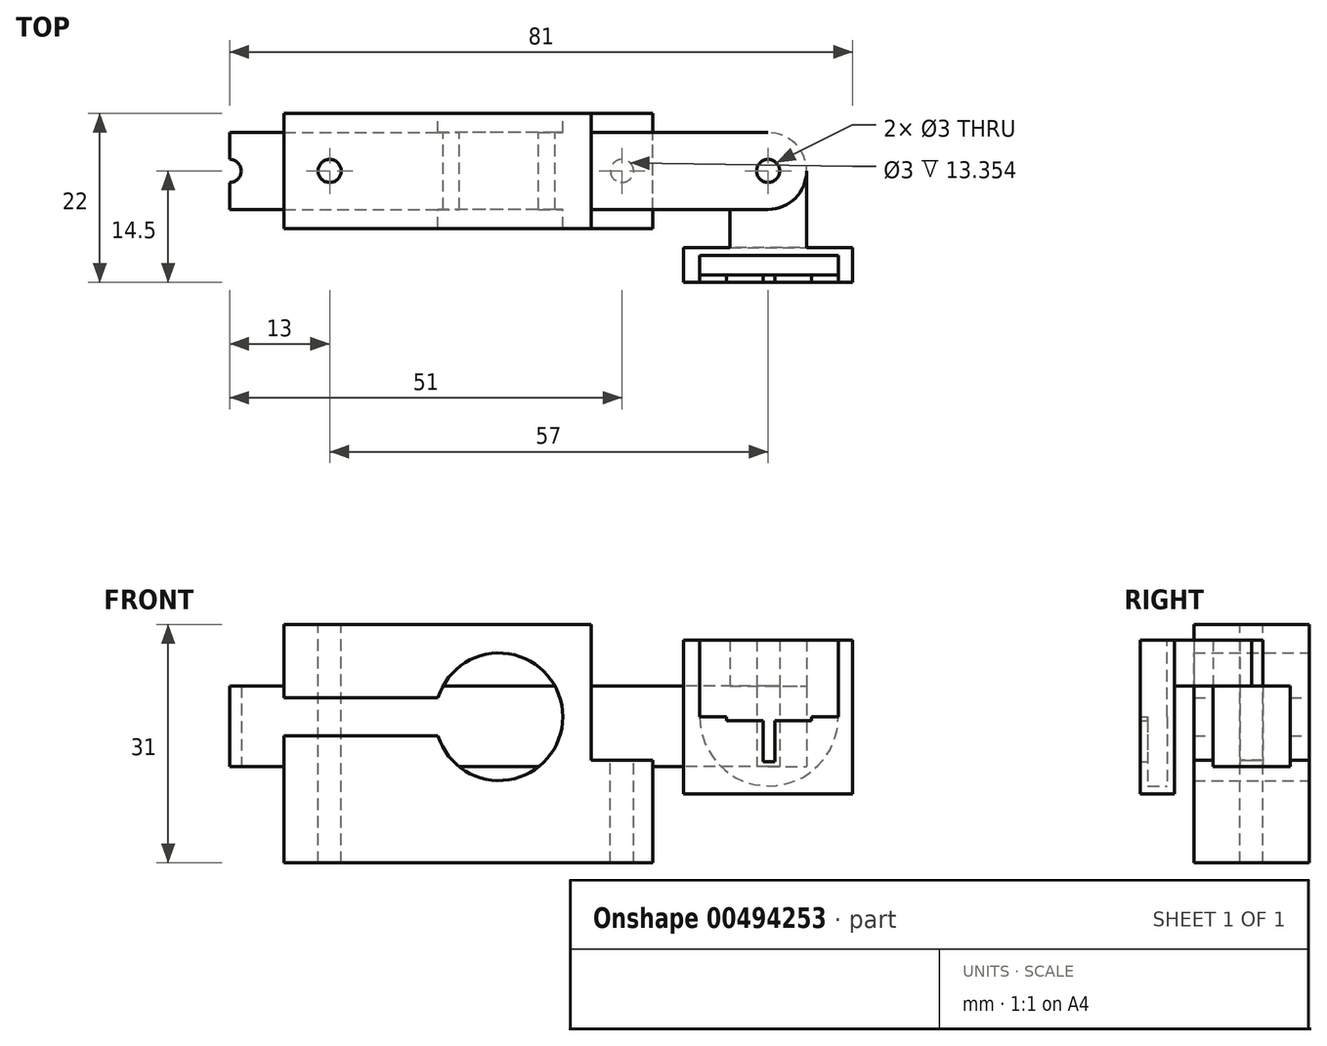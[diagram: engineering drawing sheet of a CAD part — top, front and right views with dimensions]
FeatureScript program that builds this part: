
annotation { "Feature Type Name" : "Feature", "Feature Type Description" : "" }
export const myFeature = defineFeature(function(context is Context, id is Id, definition is map)
    precondition{}
    {
        {
            var Q0;
            Q0=qCreatedBy(makeId("Top.planeOp"),FACE);
            var sketch = newSketch(context, id + "F0", { "sketchPlane" : qUnion([Q0])});
            skCircle(sketch, "E0", {"center": v(0, 0) * mm, "radius": 1.5 * mm});
            skCircle(sketch, "E1", {"center": v(0, 0) * mm, "radius": 3 * mm});
            skSolve(sketch);
        }
        {
            var Q0;
            Q0 = qSketchRegion(id + "F0", true);
            extrude(context, id + "F1", {"entities" : qUnion([Q0]), "depth" : 4 * mm, "offsetDistance" : 25 * mm});
        }
        {
            var Q0;
            Q0=qCreatedBy(makeId("Top.planeOp"),FACE);
            var sketch = newSketch(context, id + "F2", { "sketchPlane" : qUnion([Q0])});
            skLineSegment(sketch, "E2.bottom", {"start": v(35, 5) * mm, "end": v(-35, 5) * mm});
            skLineSegment(sketch, "E2.top", {"start": v(35, -5) * mm, "end": v(-35, -5) * mm});
            skLineSegment(sketch, "E2.left", {"start": v(35, 5) * mm, "end": v(35, -5) * mm});
            skLineSegment(sketch, "E2.right", {"start": v(-35, 5) * mm, "end": v(-35, -5) * mm});
            skPoint(sketch, "E2.middle", {"position": v(0, 0) * mm});
            skArc(sketch, "E3", {"start": v(35, -5) * mm, "mid": v(40, 0) * mm, "end": v(35, 5) * mm});
            skLineSegment(sketch, "E4", {"start": v(0, 15.84) * mm, "end": v(0, -21.96) * mm, "construction": true});
            skPoint(sketch, "E4.startSnap0", {"position": v(0, 5) * mm});
            skPoint(sketch, "E4.endSnap0", {"position": v(0, -5) * mm});
            skArc(sketch, "E5.MirrorCS", {"start": v(-35, -5) * mm, "mid": v(-40, 0) * mm, "end": v(-35, 5) * mm});
            skCircle(sketch, "E6", {"center": v(-35, 0) * mm, "radius": 1.5 * mm});
            skCircle(sketch, "E7.MirrorC", {"center": v(35, 0) * mm, "radius": 1.5 * mm});
            skSolve(sketch);
        }
        {
            var Q0;
            {var subQ5=sQuery(id+"F2.wireOp",EDGE,"E2.bottom");Q0=makeQuery(id+"F2.imprint","IMPRINT",FACE,{"disambiguationData":[TD([[makeQuery(id+"F2.imprint","IMPRINT",EDGE,{"derivedFrom":subQ5}),1.0]])]});}
            var Q1;
            {var subQ0=sQuery(id+"F2.wireOp",EDGE,"E5.MirrorCS");Q1=makeQuery(id+"F2.imprint","IMPRINT",FACE,{"disambiguationData":[TD([[makeQuery(id+"F2.imprint","IMPRINT",EDGE,{"derivedFrom":subQ0}),-1.0]])]});}
            var Q2;
            {var subQ0=sQuery(id+"F2.wireOp",EDGE,"E3");Q2=makeQuery(id+"F2.imprint","IMPRINT",FACE,{"disambiguationData":[TD([[makeQuery(id+"F2.imprint","IMPRINT",EDGE,{"derivedFrom":subQ0}),1.0]])]});}
            extrude(context, id + "F3", {"entities" : qUnion([Q0, Q1, Q2]), "depth" : 4 * mm, "offsetDistance" : 25 * mm});
        }
        {
            var Q0;
            Q0=makeQuery(id+"F3.opExtrude","CAP_FACE",FACE,{"disambiguationData":[OSD([sQuery(id+"F2.wireOp",EDGE,"E2.bottom"),sQuery(id+"F2.wireOp",EDGE,"E2.top"),sQuery(id+"F2.wireOp",EDGE,"E3"),sQuery(id+"F2.wireOp",EDGE,"E5.MirrorCS"),sQuery(id+"F2.wireOp",EDGE,"E6"),sQuery(id+"F2.wireOp",EDGE,"E7.MirrorC")])],"isStart":false});
            var sketch = newSketch(context, id + "F4", { "sketchPlane" : qUnion([Q0])});
            skCircle(sketch, "E8", {"center": v(35, 0) * mm, "radius": 1.5 * mm});
            skArc(sketch, "E9", {"start": v(40, 0) * mm, "mid": v(35, 5) * mm, "end": v(30, 0) * mm});
            skPoint(sketch, "E9.endSnap0", {"position": v(40, 0) * mm});
            skLineSegment(sketch, "E10.bottom", {"start": v(30, 0) * mm, "end": v(40, 0) * mm});
            skLineSegment(sketch, "E10.top", {"start": v(30, -10) * mm, "end": v(40, -10) * mm});
            skLineSegment(sketch, "E10.left", {"start": v(30, 0) * mm, "end": v(30, -10) * mm});
            skLineSegment(sketch, "E10.right", {"start": v(40, 0) * mm, "end": v(40, -10) * mm});
            skSolve(sketch);
        }
        {
            var Q0;
            {var subQ0=sQuery(id+"F4.wireOp",EDGE,"E10.bottom");var subQ3=sQuery(id+"F4.wireOp",EDGE,"E8");var subQ4=makeQuery(id+"F4.imprint","INTERSECT",VERTEX,{"disambiguationData":[OD(0.0)],"derivedFrom":[subQ3,subQ0]});Q0=makeQuery(id+"F4.imprint","IMPRINT",FACE,{"disambiguationData":[TD([[makeQuery(id+"F4.imprint","IMPRINT",EDGE,{"disambiguationData":[TD([[subQ4,-1.0]])],"derivedFrom":subQ3}),1.0]])]});}
            var Q1;
            {var subQ1=sQuery(id+"F4.wireOp",EDGE,"E10.bottom");var subQ6=sQuery(id+"F4.wireOp",EDGE,"E8");var subQ7=makeQuery(id+"F4.imprint","INTERSECT",VERTEX,{"disambiguationData":[OD(0.0)],"derivedFrom":[subQ6,subQ1]});Q1=makeQuery(id+"F4.imprint","IMPRINT",FACE,{"disambiguationData":[TD([[makeQuery(id+"F4.imprint","IMPRINT",EDGE,{"disambiguationData":[TD([[subQ7,1.0]])],"derivedFrom":subQ6}),1.0]])]});}
            var Q2;
            {var subQ2=sQuery(id+"F4.wireOp",EDGE,"E10.top");Q2=makeQuery(id+"F4.imprint","IMPRINT",FACE,{"disambiguationData":[TD([[makeQuery(id+"F4.imprint","IMPRINT",EDGE,{"derivedFrom":subQ2}),1.0]])]});}
            extrude(context, id + "F5", {"entities" : qUnion([Q0, Q1, Q2]), "depth" : 6 * mm, "offsetDistance" : 25 * mm});
        }
        {
            var Q0;
            Q0=makeQuery(id+"F5.opExtrude","SWEPT_FACE",FACE,{"disambiguationData":[OSD([sQuery(id+"F4.wireOp",EDGE,"E10.top")])]});
            var sketch = newSketch(context, id + "F6", { "sketchPlane" : qUnion([Q0])});
            skLineSegment(sketch, "E11.bottom", {"start": v(46, -10) * mm, "end": v(24, -10) * mm});
            skLineSegment(sketch, "E11.top", {"start": v(46, 10) * mm, "end": v(24, 10) * mm});
            skLineSegment(sketch, "E11.left", {"start": v(46, -10) * mm, "end": v(46, 10) * mm});
            skLineSegment(sketch, "E11.right", {"start": v(24, -10) * mm, "end": v(24, 10) * mm});
            skPoint(sketch, "E12", {"position": v(35, -10) * mm});
            skPoint(sketch, "E13", {"position": v(40, 10) * mm});
            skPoint(sketch, "E14", {"position": v(30, 10) * mm});
            skCircle(sketch, "E15", {"center": v(35.12, 0) * mm, "radius": 9 * mm});
            skLineSegment(sketch, "E16", {"start": v(26.12, 0) * mm, "end": v(26.12, 10) * mm});
            skPoint(sketch, "E16.startSnap0", {"position": v(24.12, 0) * mm});
            skLineSegment(sketch, "E17", {"start": v(44.12, 0) * mm, "end": v(44.12, 10) * mm});
            skPoint(sketch, "E17.startSnap0", {"position": v(46.12, 0) * mm});
            skPoint(sketch, "E18", {"position": v(35.12, 9) * mm});
            skSolve(sketch);
        }
        {
            var Q0;
            {var subQ3=sQuery(id+"F6.wireOp",EDGE,"E17");Q0=makeQuery(id+"F6.imprint","IMPRINT",FACE,{"disambiguationData":[TD([[makeQuery(id+"F6.imprint","IMPRINT",EDGE,{"derivedFrom":subQ3}),1.0]])]});}
            var Q1;
            {var subQ3=sQuery(id+"F6.wireOp",EDGE,"E16");Q1=makeQuery(id+"F6.imprint","IMPRINT",FACE,{"disambiguationData":[TD([[makeQuery(id+"F6.imprint","IMPRINT",EDGE,{"derivedFrom":subQ3}),-1.0]])]});}
            var Q2;
            {var subQ0=sQuery(id+"F6.wireOp",EDGE,"E11.top");var subQ1=sQuery(id+"F4.wireOp",EDGE,"E10.top");var subQ2=makeQuery(id+"F5.opExtrude","SWEPT_EDGE",EDGE,{"disambiguationData":[OSD([subQ1,sQuery(id+"F4.wireOp",EDGE,"E10.left")])]});var subQ3=makeQuery(id+"F6.imprint","INTERSECT",VERTEX,{"derivedFrom":[subQ2,subQ0]});var subQ4=makeQuery(id+"F5.opExtrude","SWEPT_EDGE",EDGE,{"disambiguationData":[OSD([subQ1,sQuery(id+"F4.wireOp",EDGE,"E10.right")])]});var subQ5=makeQuery(id+"F6.imprint","INTERSECT",VERTEX,{"derivedFrom":[subQ4,subQ0]});Q2=makeQuery(id+"F6.imprint","IMPRINT",FACE,{"disambiguationData":[TD([[makeQuery(id+"F6.imprint","IMPRINT",EDGE,{"disambiguationData":[TD([[subQ3,-1.0],[subQ5,1.0]])],"derivedFrom":subQ0}),-1.0]])]});}
            var Q3;
            {var subQ1=sQuery(id+"F4.wireOp",EDGE,"E10.top");var subQ6=makeQuery(id+"F5.opExtrude","CAP_EDGE",EDGE,{"disambiguationData":[OSD([subQ1])],"isStart":true});Q3=makeQuery(id+"F6.imprint","IMPRINT",FACE,{"disambiguationData":[TD([[makeQuery(id+"F6.imprint","IMPRINT",EDGE,{"derivedFrom":subQ6}),1.0]])]});}
            var Q4;
            {var subQ0=sQuery(id+"F4.wireOp",EDGE,"E10.top");var subQ1=makeQuery(id+"F5.opExtrude","CAP_EDGE",EDGE,{"disambiguationData":[OSD([subQ0])],"isStart":true});Q4=makeQuery(id+"F6.imprint","IMPRINT",FACE,{"disambiguationData":[TD([[makeQuery(id+"F6.imprint","IMPRINT",EDGE,{"derivedFrom":subQ1}),-1.0]])]});}
            extrude(context, id + "F7", {"entities" : qUnion([Q0, Q1, Q2, Q3, Q4]), "operationType" : NewBodyOperationType.ADD, "depth" : 1 * mm, "offsetDistance" : 25 * mm});
        }
        {
            var Q0;
            Q0=makeQuery(id+"F6.imprint","IMPRINT",FACE,{"disambiguationData":[TD([[makeQuery(id+"F6.imprint","IMPRINT",EDGE,{"derivedFrom":sQuery(id+"F6.wireOp",EDGE,"E11.bottom")}),-1.0]])]});
            extrude(context, id + "F8", {"entities" : qUnion([Q0]), "operationType" : NewBodyOperationType.ADD, "depth" : 3.5 * mm, "offsetDistance" : 25 * mm});
        }
        {
            var Q0;
            Q0=makeQuery(id+"F8.opExtrude","CAP_FACE",FACE,{"disambiguationData":[OSD([sQuery(id+"F6.wireOp",EDGE,"E11.bottom"),sQuery(id+"F6.wireOp",EDGE,"E11.top"),sQuery(id+"F6.wireOp",EDGE,"E11.left"),sQuery(id+"F6.wireOp",EDGE,"E11.right"),sQuery(id+"F6.wireOp",EDGE,"E15"),sQuery(id+"F6.wireOp",EDGE,"E16"),sQuery(id+"F6.wireOp",EDGE,"E17")])],"isStart":false});
            var sketch = newSketch(context, id + "F9", { "sketchPlane" : qUnion([Q0])});
            skLineSegment(sketch, "E19", {"start": v(26.12, 0) * mm, "end": v(44.12, 0) * mm, "construction": true});
            skLineSegment(sketch, "E20", {"start": v(35.12, -9) * mm, "end": v(35.12, -5.85) * mm, "construction": true});
            skLineSegment(sketch, "E21", {"start": v(34.37, -5.85) * mm, "end": v(35.87, -5.85) * mm});
            skLineSegment(sketch, "E22", {"start": v(34.37, -5.85) * mm, "end": v(34.37, 5.25) * mm});
            skLineSegment(sketch, "E23", {"start": v(34.37, 5.25) * mm, "end": v(35.87, 5.25) * mm});
            skLineSegment(sketch, "E24", {"start": v(35.87, 5.25) * mm, "end": v(35.87, -5.85) * mm});
            skLineSegment(sketch, "E25.bottom", {"start": v(40.67, -0.5) * mm, "end": v(29.57, -0.5) * mm});
            skLineSegment(sketch, "E25.top", {"start": v(40.67, 0.5) * mm, "end": v(29.57, 0.5) * mm});
            skLineSegment(sketch, "E25.left", {"start": v(40.67, -0.5) * mm, "end": v(40.67, 0.5) * mm});
            skLineSegment(sketch, "E25.right", {"start": v(29.57, -0.5) * mm, "end": v(29.57, 0.5) * mm});
            skPoint(sketch, "E25.middle", {"position": v(35.12, 0) * mm});
            skLineSegment(sketch, "E26", {"start": v(26.12, 0) * mm, "end": v(44.12, 0) * mm});
            skSolve(sketch);
        }
        {
            var Q0;
            {var subQ1=sQuery(id+"F9.wireOp",EDGE,"E21");Q0=makeQuery(id+"F9.imprint","IMPRINT",FACE,{"disambiguationData":[TD([[makeQuery(id+"F9.imprint","IMPRINT",EDGE,{"derivedFrom":subQ1}),-1.0]])]});}
            var Q1;
            Q1=makeQuery(id+"F9.imprint","IMPRINT",FACE,{"disambiguationData":[TD([[makeQuery(id+"F9.imprint","IMPRINT",EDGE,{"derivedFrom":makeQuery(id+"F8.opExtrude","CAP_EDGE",EDGE,{"disambiguationData":[OSD([sQuery(id+"F6.wireOp",EDGE,"E11.bottom")])],"isStart":false})}),-1.0]])]});
            extrude(context, id + "F10", {"entities" : qUnion([Q0, Q1]), "operationType" : NewBodyOperationType.ADD, "depth" : 1 * mm, "offsetDistance" : 25 * mm});
        }
        {
            var Q0;
            Q0=makeQuery(id+"F3.opExtrude","CAP_FACE",FACE,{"disambiguationData":[OSD([sQuery(id+"F2.wireOp",EDGE,"E2.bottom"),sQuery(id+"F2.wireOp",EDGE,"E2.top"),sQuery(id+"F2.wireOp",EDGE,"E3"),sQuery(id+"F2.wireOp",EDGE,"E5.MirrorCS"),sQuery(id+"F2.wireOp",EDGE,"E6"),sQuery(id+"F2.wireOp",EDGE,"E7.MirrorC")])],"isStart":true});
            extrude(context, id + "F11", {"entities" : qUnion([Q0]), "operationType" : NewBodyOperationType.ADD, "depth" : 6.5 * mm, "offsetDistance" : 25 * mm});
        }
        {
            var Q0;
            Q0=qCreatedBy(makeId("Front.planeOp"),FACE);
            var sketch = newSketch(context, id + "F12", { "sketchPlane" : qUnion([Q0])});
            skArc(sketch, "E27", {"start": v(-7.91, -2.5) * mm, "mid": v(8.3, 0) * mm, "end": v(-7.91, 2.5) * mm});
            skLineSegment(sketch, "E28", {"start": v(0, 12) * mm, "end": v(12, 12) * mm});
            skLineSegment(sketch, "E29", {"start": v(12, 12) * mm, "end": v(12, 0) * mm});
            skLineSegment(sketch, "E30", {"start": v(12, 0) * mm, "end": v(12, -12) * mm});
            skLineSegment(sketch, "E31", {"start": v(12, -12) * mm, "end": v(0, -12) * mm});
            skLineSegment(sketch, "E32", {"start": v(0, -12) * mm, "end": v(-27.91, -12) * mm});
            skLineSegment(sketch, "E33", {"start": v(0, 12) * mm, "end": v(-27.91, 12) * mm});
            skLineSegment(sketch, "E34", {"start": v(-27.91, 12) * mm, "end": v(-27.91, 2.5) * mm});
            skLineSegment(sketch, "E35", {"start": v(-7.91, 2.5) * mm, "end": v(-27.91, 2.5) * mm});
            skLineSegment(sketch, "E36", {"start": v(-7.91, -2.5) * mm, "end": v(-27.91, -2.5) * mm});
            skLineSegment(sketch, "E37.trimOffspring", {"start": v(-27.91, -2.5) * mm, "end": v(-27.91, -12) * mm});
            skSolve(sketch);
        }
        {
            var Q0;
            Q0=makeQuery(id+"F12.imprint","IMPRINT",FACE,{"disambiguationData":[TD([[makeQuery(id+"F12.imprint","IMPRINT",EDGE,{"derivedFrom":sQuery(id+"F12.wireOp",EDGE,"E27")}),-1.0]])]});
            extrude(context, id + "F13", {"entities" : qUnion([Q0]), "depth" : 15 * mm, "offsetDistance" : 25 * mm, "symmetric" : true});
        }
        {
            var Q0;
            Q0=makeQuery(id+"F13.opExtrude","SWEPT_FACE",FACE,{"disambiguationData":[OSD([sQuery(id+"F12.wireOp",EDGE,"E28"),sQuery(id+"F12.wireOp",EDGE,"E33")])]});
            var sketch = newSketch(context, id + "F14", { "sketchPlane" : qUnion([Q0])});
            skCircle(sketch, "E38", {"center": v(-22, 0) * mm, "radius": 1.5 * mm});
            skSolve(sketch);
        }
        {
            var Q0;
            Q0=makeQuery(id+"F14.imprint","IMPRINT",FACE,{"disambiguationData":[TD([[makeQuery(id+"F14.imprint","IMPRINT",EDGE,{"derivedFrom":sQuery(id+"F14.wireOp",EDGE,"E38")}),1.0]])]});
            extrude(context, id + "F15", {"entities" : qUnion([Q0]), "operationType" : NewBodyOperationType.REMOVE, "oppositeDirection" : true, "depth" : 31.6 * mm, "offsetDistance" : 25 * mm});
        }
        {
            var Q0;
            Q0=makeQuery(id+"F13.opExtrude","SWEPT_FACE",FACE,{"disambiguationData":[OSD([sQuery(id+"F12.wireOp",EDGE,"E29"),sQuery(id+"F12.wireOp",EDGE,"E30")])]});
            var sketch = newSketch(context, id + "F16", { "sketchPlane" : qUnion([Q0])});
            skLineSegment(sketch, "E39", {"start": v(-7.5, -5.65) * mm, "end": v(7.5, -5.65) * mm});
            skLineSegment(sketch, "E40", {"start": v(7.5, -5.65) * mm, "end": v(7.5, -12) * mm});
            skLineSegment(sketch, "E41", {"start": v(7.5, -12) * mm, "end": v(-7.5, -12) * mm});
            skLineSegment(sketch, "E42", {"start": v(-7.5, -12) * mm, "end": v(-7.5, -5.65) * mm});
            skSolve(sketch);
        }
        {
            var Q0;
            Q0=makeQuery(id+"F16.imprint","IMPRINT",FACE,{"disambiguationData":[TD([[makeQuery(id+"F16.imprint","IMPRINT",EDGE,{"derivedFrom":sQuery(id+"F16.wireOp",EDGE,"E39")}),-1.0]])]});
            extrude(context, id + "F17", {"entities" : qUnion([Q0]), "operationType" : NewBodyOperationType.ADD, "depth" : 8 * mm, "offsetDistance" : 25 * mm});
        }
        {
            var Q0;
            Q0=makeQuery(id+"F17.opExtrude","SWEPT_FACE",FACE,{"disambiguationData":[OSD([sQuery(id+"F16.wireOp",EDGE,"E39")])]});
            var sketch = newSketch(context, id + "F18", { "sketchPlane" : qUnion([Q0])});
            skCircle(sketch, "E43", {"center": v(16, 0) * mm, "radius": 1.5 * mm});
            skSolve(sketch);
        }
        {
            var Q0;
            Q0=makeQuery(id+"F18.imprint","IMPRINT",FACE,{"disambiguationData":[TD([[makeQuery(id+"F18.imprint","IMPRINT",EDGE,{"derivedFrom":sQuery(id+"F18.wireOp",EDGE,"E43")}),1.0]])]});
            extrude(context, id + "F19", {"entities" : qUnion([Q0]), "operationType" : NewBodyOperationType.REMOVE, "oppositeDirection" : true, "depth" : 25 * mm, "offsetDistance" : 25 * mm});
        }
        {
            var Q0;
            Q0=makeQuery(id+"F17.boolean.opBoolean","MERGE",FACE,{"derivedFrom":[makeQuery(id+"F13.opExtrude","SWEPT_FACE",FACE,{"disambiguationData":[OSD([sQuery(id+"F12.wireOp",EDGE,"E31"),sQuery(id+"F12.wireOp",EDGE,"E32")])]}),makeQuery(id+"F17.opExtrude","SWEPT_FACE",FACE,{"disambiguationData":[OSD([sQuery(id+"F16.wireOp",EDGE,"E41")])]})]});
            extrude(context, id + "F20", {"entities" : qUnion([Q0]), "operationType" : NewBodyOperationType.ADD, "depth" : 7 * mm, "offsetDistance" : 25 * mm});
        }
    });
